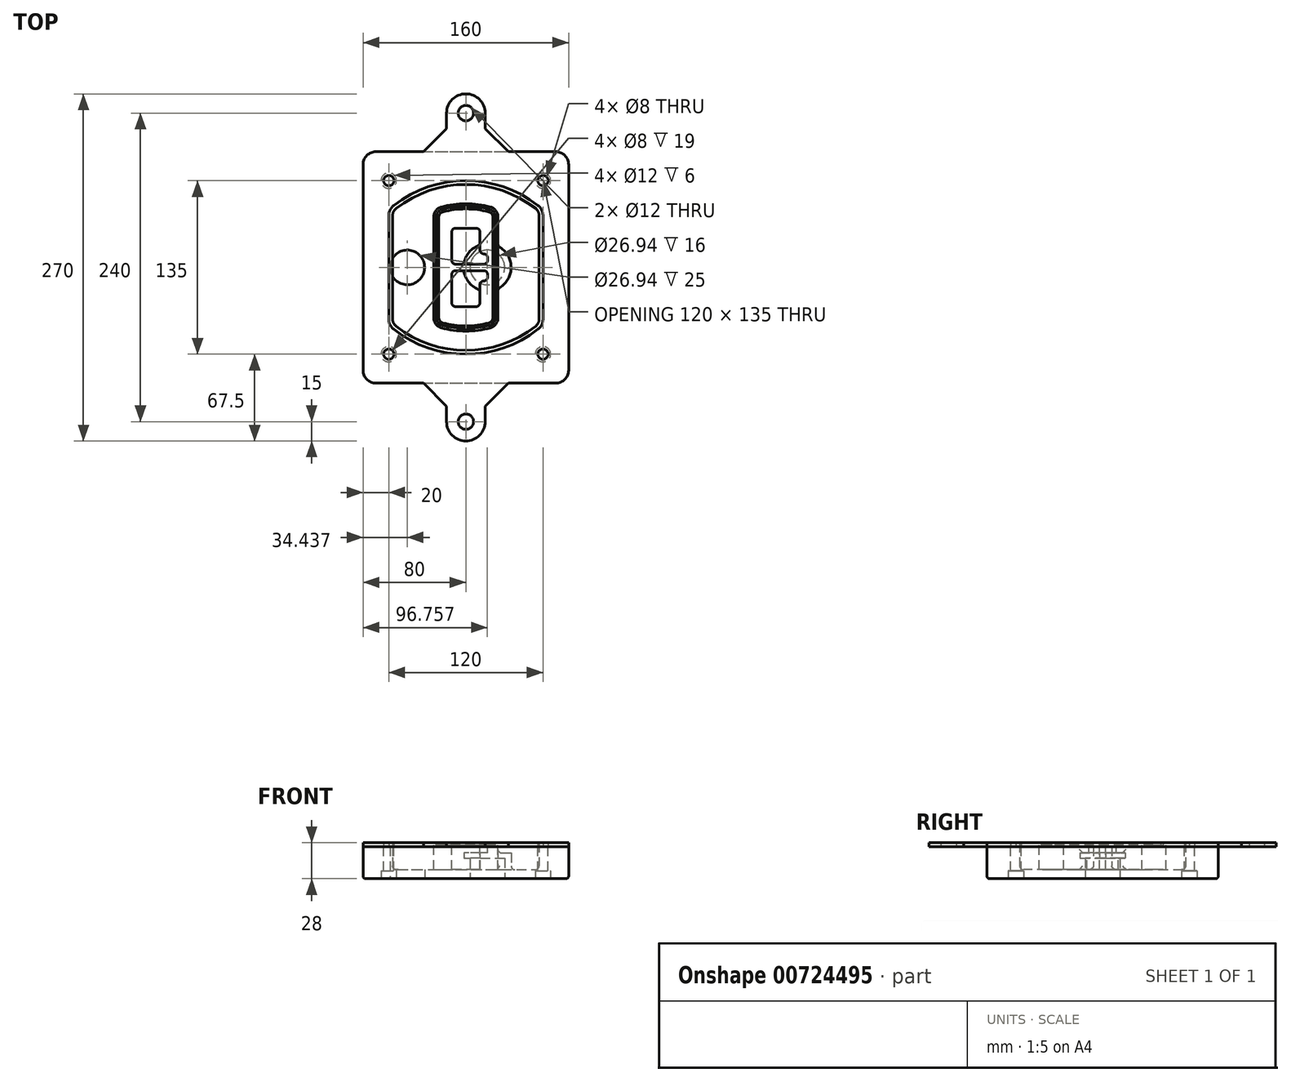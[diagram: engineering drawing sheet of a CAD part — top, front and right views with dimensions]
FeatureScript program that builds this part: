
annotation { "Feature Type Name" : "Feature", "Feature Type Description" : "" }
export const myFeature = defineFeature(function(context is Context, id is Id, definition is map)
    precondition{}
    {
        {
            var Q0;
            Q0=qCreatedBy(makeId("Top.planeOp"),FACE);
            var sketch = newSketch(context, id + "F0", { "sketchPlane" : qUnion([Q0])});
            skPoint(sketch, "E0.rect.middle", {"position": v(0, 0) * mm});
            skLineSegment(sketch, "E1.bottom", {"start": v(-70, -90) * mm, "end": v(70, -90) * mm});
            skLineSegment(sketch, "E1.top", {"start": v(-70, 90) * mm, "end": v(70, 90) * mm});
            skLineSegment(sketch, "E1.left", {"start": v(-80, -80) * mm, "end": v(-80, 80) * mm});
            skLineSegment(sketch, "E1.right", {"start": v(80, -80) * mm, "end": v(80, 80) * mm});
            skLineSegment(sketch, "E2", {"start": v(-80, 90) * mm, "end": v(80, -90) * mm, "construction": true});
            skLineSegment(sketch, "E3", {"start": v(80, 90) * mm, "end": v(-80, -90) * mm, "construction": true});
            skCircle(sketch, "E4", {"center": v(-60, 67.5) * mm, "radius": 4 * mm});
            skCircle(sketch, "E5", {"center": v(60, 67.5) * mm, "radius": 4 * mm});
            skCircle(sketch, "E6", {"center": v(60, -67.5) * mm, "radius": 4 * mm});
            skCircle(sketch, "E7", {"center": v(-60, -67.5) * mm, "radius": 4 * mm});
            skLineSegment(sketch, "E8", {"start": v(-60, 67.5) * mm, "end": v(60, 67.5) * mm, "construction": true});
            skLineSegment(sketch, "E9", {"start": v(60, 67.5) * mm, "end": v(60, -67.5) * mm, "construction": true});
            skLineSegment(sketch, "E10", {"start": v(60, -67.5) * mm, "end": v(-60, -67.5) * mm, "construction": true});
            skLineSegment(sketch, "E11", {"start": v(-60, -67.5) * mm, "end": v(-60, 67.5) * mm, "construction": true});
            skLineSegment(sketch, "E12", {"start": v(-60, 40.3) * mm, "end": v(-60, -40.3) * mm});
            skLineSegment(sketch, "E13", {"start": v(60, 40.3) * mm, "end": v(60, -40.3) * mm});
            skArc(sketch, "E14", {"start": v(56.15, 48.18) * mm, "mid": v(0, 67.5) * mm, "end": v(-56.15, 48.18) * mm});
            skArc(sketch, "E15", {"start": v(-56.15, -48.18) * mm, "mid": v(0, -67.5) * mm, "end": v(56.15, -48.18) * mm});
            skLineSegment(sketch, "E16", {"start": v(-60, 0) * mm, "end": v(60, 0) * mm, "construction": true});
            skPoint(sketch, "E17.visualSharp", {"position": v(-60, -45) * mm});
            skArc(sketch, "E17.filletArc", {"start": v(-60, -40.3) * mm, "mid": v(-58.99, -44.68) * mm, "end": v(-56.15, -48.18) * mm});
            skPoint(sketch, "E18.visualSharp", {"position": v(-60, 45) * mm});
            skArc(sketch, "E18.filletArc", {"start": v(-56.15, 48.18) * mm, "mid": v(-58.99, 44.68) * mm, "end": v(-60, 40.3) * mm});
            skPoint(sketch, "E19.visualSharp", {"position": v(60, 45) * mm});
            skArc(sketch, "E19.filletArc", {"start": v(60, 40.3) * mm, "mid": v(58.99, 44.68) * mm, "end": v(56.15, 48.18) * mm});
            skPoint(sketch, "E20.visualSharp", {"position": v(60, -45) * mm});
            skArc(sketch, "E20.filletArc", {"start": v(56.15, -48.18) * mm, "mid": v(58.99, -44.68) * mm, "end": v(60, -40.3) * mm});
            skPoint(sketch, "E21.visualSharp", {"position": v(-80, 90) * mm});
            skArc(sketch, "E21.filletArc", {"start": v(-70, 90) * mm, "mid": v(-77.07, 87.07) * mm, "end": v(-80, 80) * mm});
            skPoint(sketch, "E22.visualSharp", {"position": v(80, 90) * mm});
            skArc(sketch, "E22.filletArc", {"start": v(80, 80) * mm, "mid": v(77.07, 87.07) * mm, "end": v(70, 90) * mm});
            skPoint(sketch, "E23.visualSharp", {"position": v(80, -90) * mm});
            skArc(sketch, "E23.filletArc", {"start": v(70, -90) * mm, "mid": v(77.07, -87.07) * mm, "end": v(80, -80) * mm});
            skPoint(sketch, "E24.visualSharp", {"position": v(-80, -90) * mm});
            skArc(sketch, "E24.filletArc", {"start": v(-80, -80) * mm, "mid": v(-77.07, -87.07) * mm, "end": v(-70, -90) * mm});
            skArc(sketch, "E25.0", {"start": v(57, 40.3) * mm, "mid": v(56.3, 43.36) * mm, "end": v(54.3, 45.81) * mm});
            skLineSegment(sketch, "E25.1", {"start": v(57, 40.3) * mm, "end": v(57, -40.3) * mm});
            skArc(sketch, "E25.2", {"start": v(54.3, -45.81) * mm, "mid": v(56.3, -43.36) * mm, "end": v(57, -40.3) * mm});
            skArc(sketch, "E25.3", {"start": v(-54.3, -45.81) * mm, "mid": v(0, -64.5) * mm, "end": v(54.3, -45.81) * mm});
            skArc(sketch, "E25.4", {"start": v(-57, -40.3) * mm, "mid": v(-56.3, -43.36) * mm, "end": v(-54.3, -45.81) * mm});
            skArc(sketch, "E25.5", {"start": v(54.3, 45.81) * mm, "mid": v(0, 64.5) * mm, "end": v(-54.3, 45.81) * mm});
            skLineSegment(sketch, "E25.6", {"start": v(-57, 40.3) * mm, "end": v(-57, -40.3) * mm});
            skArc(sketch, "E25.7", {"start": v(-54.3, 45.81) * mm, "mid": v(-56.3, 43.36) * mm, "end": v(-57, 40.3) * mm});
            skArc(sketch, "E26.0", {"start": v(-58.62, 51.33) * mm, "mid": v(-62.58, 46.43) * mm, "end": v(-64, 40.3) * mm});
            skArc(sketch, "E26.1", {"start": v(58.62, 51.33) * mm, "mid": v(0, 71.5) * mm, "end": v(-58.62, 51.33) * mm});
            skArc(sketch, "E26.2", {"start": v(64, 40.3) * mm, "mid": v(62.58, 46.43) * mm, "end": v(58.62, 51.33) * mm});
            skLineSegment(sketch, "E26.3", {"start": v(64, 40.3) * mm, "end": v(64, -40.3) * mm});
            skArc(sketch, "E26.4", {"start": v(58.62, -51.33) * mm, "mid": v(62.58, -46.43) * mm, "end": v(64, -40.3) * mm});
            skLineSegment(sketch, "E26.5", {"start": v(-64, 40.3) * mm, "end": v(-64, -40.3) * mm});
            skArc(sketch, "E26.6", {"start": v(-58.62, -51.33) * mm, "mid": v(0, -71.5) * mm, "end": v(58.62, -51.33) * mm});
            skArc(sketch, "E26.7", {"start": v(-64, -40.3) * mm, "mid": v(-62.58, -46.43) * mm, "end": v(-58.62, -51.33) * mm});
            skSolve(sketch);
        }
        {
            var Q0;
            Q0=makeQuery(id+"F0.imprint","IMPRINT",FACE,{"disambiguationData":[TD([[makeQuery(id+"F0.imprint","IMPRINT",EDGE,{"derivedFrom":sQuery(id+"F0.wireOp",EDGE,"E1.bottom")}),1.0]])]});
            var Q1;
            Q1=makeQuery(id+"F0.imprint","IMPRINT",FACE,{"disambiguationData":[TD([[makeQuery(id+"F0.imprint","IMPRINT",EDGE,{"derivedFrom":sQuery(id+"F0.wireOp",EDGE,"E12")}),1.0]])]});
            var Q2;
            Q2=makeQuery(id+"F0.imprint","IMPRINT",FACE,{"disambiguationData":[TD([[makeQuery(id+"F0.imprint","IMPRINT",EDGE,{"derivedFrom":sQuery(id+"F0.wireOp",EDGE,"E25.0")}),1.0]])]});
            var Q3;
            Q3=makeQuery(id+"F0.imprint","IMPRINT",FACE,{"disambiguationData":[TD([[makeQuery(id+"F0.imprint","IMPRINT",EDGE,{"derivedFrom":sQuery(id+"F0.wireOp",EDGE,"E12")}),-1.0]])]});
            extrude(context, id + "F1", {"entities" : qUnion([Q0, Q1, Q2, Q3]), "oppositeDirection" : true, "depth" : 25 * mm});
        }
        {
            var Q0;
            Q0=makeQuery(id+"F0.imprint","IMPRINT",FACE,{"disambiguationData":[TD([[makeQuery(id+"F0.imprint","IMPRINT",EDGE,{"derivedFrom":sQuery(id+"F0.wireOp",EDGE,"E12")}),1.0]])]});
            extrude(context, id + "F2", {"entities" : qUnion([Q0]), "operationType" : NewBodyOperationType.ADD, "depth" : 3 * mm});
        }
        {
            var Q0;
            Q0=makeQuery(id+"F0.imprint","IMPRINT",FACE,{"disambiguationData":[TD([[makeQuery(id+"F0.imprint","IMPRINT",EDGE,{"derivedFrom":sQuery(id+"F0.wireOp",EDGE,"E25.0")}),1.0]])]});
            extrude(context, id + "F3", {"entities" : qUnion([Q0]), "operationType" : NewBodyOperationType.REMOVE, "oppositeDirection" : true, "depth" : 18 * mm});
        }
        {
            var Q0;
            Q0=makeQuery(id+"F2.opExtrude","CAP_FACE",FACE,{"disambiguationData":[OSD([sQuery(id+"F0.wireOp",EDGE,"E12"),sQuery(id+"F0.wireOp",EDGE,"E13"),sQuery(id+"F0.wireOp",EDGE,"E14"),sQuery(id+"F0.wireOp",EDGE,"E15"),sQuery(id+"F0.wireOp",EDGE,"E17.filletArc"),sQuery(id+"F0.wireOp",EDGE,"E18.filletArc"),sQuery(id+"F0.wireOp",EDGE,"E19.filletArc"),sQuery(id+"F0.wireOp",EDGE,"E20.filletArc"),sQuery(id+"F0.wireOp",EDGE,"E25.0"),sQuery(id+"F0.wireOp",EDGE,"E25.1"),sQuery(id+"F0.wireOp",EDGE,"E25.2"),sQuery(id+"F0.wireOp",EDGE,"E25.3"),sQuery(id+"F0.wireOp",EDGE,"E25.4"),sQuery(id+"F0.wireOp",EDGE,"E25.5"),sQuery(id+"F0.wireOp",EDGE,"E25.6"),sQuery(id+"F0.wireOp",EDGE,"E25.7")])],"isStart":false});
            var sketch = newSketch(context, id + "F4", { "sketchPlane" : qUnion([Q0])});
            skArc(sketch, "E27.0", {"start": v(-19.08, -46.97) * mm, "mid": v(0, -49.5) * mm, "end": v(19.08, -46.97) * mm});
            skArc(sketch, "E28.0", {"start": v(19.08, 46.97) * mm, "mid": v(0, 49.5) * mm, "end": v(-19.08, 46.97) * mm});
            skLineSegment(sketch, "E29", {"start": v(-25, 39.25) * mm, "end": v(-25, -39.25) * mm});
            skLineSegment(sketch, "E30", {"start": v(25, 39.25) * mm, "end": v(25, -39.25) * mm});
            skLineSegment(sketch, "E31", {"start": v(-25, 45.1) * mm, "end": v(25, 45.1) * mm, "construction": true});
            skLineSegment(sketch, "E32", {"start": v(-25, -45.1) * mm, "end": v(25, -45.1) * mm, "construction": true});
            skPoint(sketch, "E33.visualSharp", {"position": v(-25, 45.1) * mm});
            skArc(sketch, "E33.filletArc", {"start": v(-19.08, 46.97) * mm, "mid": v(-23.35, 44.11) * mm, "end": v(-25, 39.25) * mm});
            skPoint(sketch, "E34.visualSharp", {"position": v(25, 45.1) * mm});
            skArc(sketch, "E34.filletArc", {"start": v(25, 39.25) * mm, "mid": v(23.35, 44.11) * mm, "end": v(19.08, 46.97) * mm});
            skPoint(sketch, "E35.visualSharp", {"position": v(25, -45.1) * mm});
            skArc(sketch, "E35.filletArc", {"start": v(19.08, -46.97) * mm, "mid": v(23.35, -44.11) * mm, "end": v(25, -39.25) * mm});
            skPoint(sketch, "E36.visualSharp", {"position": v(-25, -45.1) * mm});
            skArc(sketch, "E36.filletArc", {"start": v(-25, -39.25) * mm, "mid": v(-23.35, -44.11) * mm, "end": v(-19.08, -46.97) * mm});
            skArc(sketch, "E37.0", {"start": v(54.3, 45.81) * mm, "mid": v(0, 64.5) * mm, "end": v(-54.3, 45.81) * mm});
            skArc(sketch, "E37.1", {"start": v(-54.3, 45.81) * mm, "mid": v(-56.3, 43.36) * mm, "end": v(-57, 40.3) * mm});
            skLineSegment(sketch, "E37.2", {"start": v(-57, 40.3) * mm, "end": v(-57, -40.3) * mm});
            skArc(sketch, "E37.3", {"start": v(-57, -40.3) * mm, "mid": v(-56.3, -43.36) * mm, "end": v(-54.3, -45.81) * mm});
            skArc(sketch, "E37.4", {"start": v(-54.3, -45.81) * mm, "mid": v(0, -64.5) * mm, "end": v(54.3, -45.81) * mm});
            skArc(sketch, "E37.5", {"start": v(54.3, -45.81) * mm, "mid": v(56.3, -43.36) * mm, "end": v(57, -40.3) * mm});
            skLineSegment(sketch, "E37.6", {"start": v(57, 40.3) * mm, "end": v(57, -40.3) * mm});
            skArc(sketch, "E37.7", {"start": v(57, 40.3) * mm, "mid": v(56.3, 43.36) * mm, "end": v(54.3, 45.81) * mm});
            skLineSegment(sketch, "E38.0", {"start": v(23, 39.25) * mm, "end": v(23, -39.25) * mm});
            skArc(sketch, "E38.1", {"start": v(18.56, -45.04) * mm, "mid": v(21.76, -42.9) * mm, "end": v(23, -39.25) * mm});
            skArc(sketch, "E38.2", {"start": v(-18.56, -45.04) * mm, "mid": v(0, -47.5) * mm, "end": v(18.56, -45.04) * mm});
            skArc(sketch, "E38.3", {"start": v(-23, -39.25) * mm, "mid": v(-21.76, -42.9) * mm, "end": v(-18.56, -45.04) * mm});
            skLineSegment(sketch, "E38.4", {"start": v(-23, 39.25) * mm, "end": v(-23, -39.25) * mm});
            skArc(sketch, "E38.5", {"start": v(23, 39.25) * mm, "mid": v(21.76, 42.9) * mm, "end": v(18.56, 45.04) * mm});
            skArc(sketch, "E38.6", {"start": v(-18.56, 45.04) * mm, "mid": v(-21.76, 42.9) * mm, "end": v(-23, 39.25) * mm});
            skArc(sketch, "E38.7", {"start": v(18.56, 45.04) * mm, "mid": v(0, 47.5) * mm, "end": v(-18.56, 45.04) * mm});
            skArc(sketch, "E39.0", {"start": v(21, 39.25) * mm, "mid": v(20.18, 41.68) * mm, "end": v(18.04, 43.1) * mm});
            skLineSegment(sketch, "E39.1", {"start": v(21, 39.25) * mm, "end": v(21, -39.25) * mm});
            skArc(sketch, "E39.2", {"start": v(18.04, -43.1) * mm, "mid": v(20.18, -41.68) * mm, "end": v(21, -39.25) * mm});
            skArc(sketch, "E39.3", {"start": v(-18.04, -43.1) * mm, "mid": v(0, -45.5) * mm, "end": v(18.04, -43.1) * mm});
            skArc(sketch, "E39.4", {"start": v(-21, -39.25) * mm, "mid": v(-20.18, -41.68) * mm, "end": v(-18.04, -43.1) * mm});
            skArc(sketch, "E39.5", {"start": v(18.04, 43.1) * mm, "mid": v(0, 45.5) * mm, "end": v(-18.04, 43.1) * mm});
            skLineSegment(sketch, "E39.6", {"start": v(-21, 39.25) * mm, "end": v(-21, -39.25) * mm});
            skArc(sketch, "E39.7", {"start": v(-18.04, 43.1) * mm, "mid": v(-20.18, 41.68) * mm, "end": v(-21, 39.25) * mm});
            skLineSegment(sketch, "E40", {"start": v(-25, 0) * mm, "end": v(25, 0) * mm, "construction": true});
            skLineSegment(sketch, "E41", {"start": v(-11, 5.5) * mm, "end": v(-11, 27.5) * mm});
            skLineSegment(sketch, "E42", {"start": v(-8, 30.5) * mm, "end": v(8, 30.5) * mm});
            skLineSegment(sketch, "E43", {"start": v(11, 27.5) * mm, "end": v(11, 13.5) * mm});
            skLineSegment(sketch, "E44", {"start": v(14, 10.5) * mm, "end": v(14, 10.5) * mm});
            skLineSegment(sketch, "E45", {"start": v(17, 7.5) * mm, "end": v(17, 5.5) * mm});
            skLineSegment(sketch, "E46", {"start": v(14, 2.5) * mm, "end": v(-8, 2.5) * mm});
            skPoint(sketch, "E47.visualSharp", {"position": v(-11, 30.5) * mm});
            skArc(sketch, "E47.filletArc", {"start": v(-8, 30.5) * mm, "mid": v(-10.12, 29.62) * mm, "end": v(-11, 27.5) * mm});
            skPoint(sketch, "E48.visualSharp", {"position": v(11, 30.5) * mm});
            skArc(sketch, "E48.filletArc", {"start": v(11, 27.5) * mm, "mid": v(10.12, 29.62) * mm, "end": v(8, 30.5) * mm});
            skPoint(sketch, "E49.visualSharp", {"position": v(11, 10.5) * mm});
            skArc(sketch, "E49.filletArc", {"start": v(11, 13.5) * mm, "mid": v(11.88, 11.38) * mm, "end": v(14, 10.5) * mm});
            skPoint(sketch, "E50.visualSharp", {"position": v(17, 10.5) * mm});
            skArc(sketch, "E50.filletArc", {"start": v(17, 7.5) * mm, "mid": v(16.12, 9.62) * mm, "end": v(14, 10.5) * mm});
            skPoint(sketch, "E51.visualSharp", {"position": v(17, 2.5) * mm});
            skArc(sketch, "E51.filletArc", {"start": v(14, 2.5) * mm, "mid": v(16.12, 3.38) * mm, "end": v(17, 5.5) * mm});
            skPoint(sketch, "E52.visualSharp", {"position": v(-11, 2.5) * mm});
            skArc(sketch, "E52.filletArc", {"start": v(-11, 5.5) * mm, "mid": v(-10.12, 3.38) * mm, "end": v(-8, 2.5) * mm});
            skLineSegment(sketch, "E53.0.MirrorCS", {"start": v(14, -2.5) * mm, "end": v(-8, -2.5) * mm});
            skArc(sketch, "E54.0.MirrorCS", {"start": v(-11, -5.5) * mm, "mid": v(-10.12, -3.38) * mm, "end": v(-8, -2.5) * mm});
            skLineSegment(sketch, "E55.0.MirrorCS", {"start": v(-11, -5.5) * mm, "end": v(-11, -27.5) * mm});
            skArc(sketch, "E56.0.MirrorCS", {"start": v(-8, -30.5) * mm, "mid": v(-10.12, -29.62) * mm, "end": v(-11, -27.5) * mm});
            skLineSegment(sketch, "E57.0.MirrorCS", {"start": v(-8, -30.5) * mm, "end": v(8, -30.5) * mm});
            skArc(sketch, "E58.0.MirrorCS", {"start": v(11, -27.5) * mm, "mid": v(10.12, -29.62) * mm, "end": v(8, -30.5) * mm});
            skLineSegment(sketch, "E59.0.MirrorCS", {"start": v(11, -27.5) * mm, "end": v(11, -13.5) * mm});
            skArc(sketch, "E60.0.MirrorCS", {"start": v(11, -13.5) * mm, "mid": v(11.88, -11.38) * mm, "end": v(14, -10.5) * mm});
            skArc(sketch, "E61.0.MirrorCS", {"start": v(17, -7.5) * mm, "mid": v(16.12, -9.62) * mm, "end": v(14, -10.5) * mm});
            skLineSegment(sketch, "E62.0.MirrorCS", {"start": v(17, -7.5) * mm, "end": v(17, -5.5) * mm});
            skArc(sketch, "E63.0.MirrorCS", {"start": v(14, -2.5) * mm, "mid": v(16.12, -3.38) * mm, "end": v(17, -5.5) * mm});
            skSolve(sketch);
        }
        {
            var Q0;
            Q0=makeQuery(id+"F4.imprint","IMPRINT",FACE,{"disambiguationData":[TD([[makeQuery(id+"F4.imprint","IMPRINT",EDGE,{"derivedFrom":sQuery(id+"F4.wireOp",EDGE,"E27.0")}),1.0]])]});
            var Q1;
            Q1=makeQuery(id+"F4.imprint","IMPRINT",FACE,{"disambiguationData":[TD([[makeQuery(id+"F4.imprint","IMPRINT",EDGE,{"derivedFrom":sQuery(id+"F4.wireOp",EDGE,"E38.0")}),-1.0]])]});
            var Q2;
            Q2=makeQuery(id+"F4.imprint","IMPRINT",FACE,{"disambiguationData":[TD([[makeQuery(id+"F4.imprint","IMPRINT",EDGE,{"derivedFrom":sQuery(id+"F4.wireOp",EDGE,"E39.0")}),1.0]])]});
            extrude(context, id + "F5", {"entities" : qUnion([Q0, Q1, Q2]), "operationType" : NewBodyOperationType.ADD, "endBound" : BoundingType.UP_TO_NEXT, "oppositeDirection" : true, "depth" : 25 * mm});
        }
        {
            var Q0;
            Q0=makeQuery(id+"F4.imprint","IMPRINT",FACE,{"disambiguationData":[TD([[makeQuery(id+"F4.imprint","IMPRINT",EDGE,{"derivedFrom":sQuery(id+"F4.wireOp",EDGE,"E38.0")}),-1.0]])]});
            extrude(context, id + "F6", {"entities" : qUnion([Q0]), "operationType" : NewBodyOperationType.REMOVE, "oppositeDirection" : true, "depth" : 2 * mm});
        }
        {
            var Q0;
            Q0=makeQuery(id+"F1.opExtrude","CAP_FACE",FACE,{"disambiguationData":[OSD([sQuery(id+"F0.wireOp",EDGE,"E1.bottom"),sQuery(id+"F0.wireOp",EDGE,"E1.top"),sQuery(id+"F0.wireOp",EDGE,"E1.left"),sQuery(id+"F0.wireOp",EDGE,"E1.right"),sQuery(id+"F0.wireOp",EDGE,"E4"),sQuery(id+"F0.wireOp",EDGE,"E5"),sQuery(id+"F0.wireOp",EDGE,"E6"),sQuery(id+"F0.wireOp",EDGE,"E7"),sQuery(id+"F0.wireOp",EDGE,"E21.filletArc"),sQuery(id+"F0.wireOp",EDGE,"E22.filletArc"),sQuery(id+"F0.wireOp",EDGE,"E23.filletArc"),sQuery(id+"F0.wireOp",EDGE,"E24.filletArc")])],"isStart":false});
            var sketch = newSketch(context, id + "F7", { "sketchPlane" : qUnion([Q0])});
            skCircle(sketch, "E64", {"center": v(16.76, 0) * mm, "radius": 13.47 * mm});
            skCircle(sketch, "E65", {"center": v(-45.56, 0) * mm, "radius": 13.47 * mm});
            skLineSegment(sketch, "E66", {"start": v(80, 0) * mm, "end": v(-80, 0) * mm});
            skCircle(sketch, "E67", {"center": v(16.76, 0) * mm, "radius": 18.47 * mm});
            skCircle(sketch, "E68", {"center": v(60, -67.5) * mm, "radius": 6 * mm});
            skCircle(sketch, "E69", {"center": v(-60, -67.5) * mm, "radius": 6 * mm});
            skCircle(sketch, "E70", {"center": v(-60, 67.5) * mm, "radius": 6 * mm});
            skCircle(sketch, "E71", {"center": v(60, 67.5) * mm, "radius": 6 * mm});
            skSolve(sketch);
        }
        {
            var Q0;
            {var subQ1=sQuery(id+"F7.wireOp",EDGE,"E66");var subQ4=sQuery(id+"F7.wireOp",EDGE,"E64");var subQ6=makeQuery(id+"F7.imprint","INTERSECT",VERTEX,{"disambiguationData":[OD(0.0)],"derivedFrom":[subQ4,subQ1]});Q0=makeQuery(id+"F7.imprint","IMPRINT",FACE,{"disambiguationData":[TD([[makeQuery(id+"F7.imprint","IMPRINT",EDGE,{"disambiguationData":[TD([[subQ6,-1.0]])],"derivedFrom":subQ4}),-1.0]])]});}
            var Q1;
            {var subQ0=sQuery(id+"F7.wireOp",EDGE,"E66");var subQ1=sQuery(id+"F7.wireOp",EDGE,"E64");var subQ3=makeQuery(id+"F7.imprint","INTERSECT",VERTEX,{"disambiguationData":[OD(0.0)],"derivedFrom":[subQ1,subQ0]});Q1=makeQuery(id+"F7.imprint","IMPRINT",FACE,{"disambiguationData":[TD([[makeQuery(id+"F7.imprint","IMPRINT",EDGE,{"disambiguationData":[TD([[subQ3,-1.0]])],"derivedFrom":subQ1}),1.0]])]});}
            var Q2;
            {var subQ0=sQuery(id+"F7.wireOp",EDGE,"E66");var subQ1=sQuery(id+"F7.wireOp",EDGE,"E64");var subQ3=makeQuery(id+"F7.imprint","INTERSECT",VERTEX,{"disambiguationData":[OD(0.0)],"derivedFrom":[subQ1,subQ0]});Q2=makeQuery(id+"F7.imprint","IMPRINT",FACE,{"disambiguationData":[TD([[makeQuery(id+"F7.imprint","IMPRINT",EDGE,{"disambiguationData":[TD([[subQ3,1.0]])],"derivedFrom":subQ1}),1.0]])]});}
            var Q3;
            {var subQ1=sQuery(id+"F7.wireOp",EDGE,"E66");var subQ4=sQuery(id+"F7.wireOp",EDGE,"E64");var subQ6=makeQuery(id+"F7.imprint","INTERSECT",VERTEX,{"disambiguationData":[OD(0.0)],"derivedFrom":[subQ4,subQ1]});Q3=makeQuery(id+"F7.imprint","IMPRINT",FACE,{"disambiguationData":[TD([[makeQuery(id+"F7.imprint","IMPRINT",EDGE,{"disambiguationData":[TD([[subQ6,1.0]])],"derivedFrom":subQ4}),-1.0]])]});}
            extrude(context, id + "F8", {"entities" : qUnion([Q0, Q1, Q2, Q3]), "operationType" : NewBodyOperationType.ADD, "oppositeDirection" : true, "depth" : 20 * mm});
        }
        {
            var Q0;
            {var subQ0=sQuery(id+"F7.wireOp",EDGE,"E66");var subQ1=sQuery(id+"F7.wireOp",EDGE,"E64");var subQ3=makeQuery(id+"F7.imprint","INTERSECT",VERTEX,{"disambiguationData":[OD(0.0)],"derivedFrom":[subQ1,subQ0]});Q0=makeQuery(id+"F7.imprint","IMPRINT",FACE,{"disambiguationData":[TD([[makeQuery(id+"F7.imprint","IMPRINT",EDGE,{"disambiguationData":[TD([[subQ3,-1.0]])],"derivedFrom":subQ1}),1.0]])]});}
            var Q1;
            {var subQ0=sQuery(id+"F7.wireOp",EDGE,"E66");var subQ1=sQuery(id+"F7.wireOp",EDGE,"E64");var subQ3=makeQuery(id+"F7.imprint","INTERSECT",VERTEX,{"disambiguationData":[OD(0.0)],"derivedFrom":[subQ1,subQ0]});Q1=makeQuery(id+"F7.imprint","IMPRINT",FACE,{"disambiguationData":[TD([[makeQuery(id+"F7.imprint","IMPRINT",EDGE,{"disambiguationData":[TD([[subQ3,1.0]])],"derivedFrom":subQ1}),1.0]])]});}
            extrude(context, id + "F9", {"entities" : qUnion([Q0, Q1]), "operationType" : NewBodyOperationType.REMOVE, "oppositeDirection" : true, "depth" : 16 * mm});
        }
        {
            var Q0;
            {var subQ0=sQuery(id+"F7.wireOp",EDGE,"E66");var subQ1=sQuery(id+"F7.wireOp",EDGE,"E65");var subQ3=makeQuery(id+"F7.imprint","INTERSECT",VERTEX,{"disambiguationData":[OD(0.0)],"derivedFrom":[subQ1,subQ0]});Q0=makeQuery(id+"F7.imprint","IMPRINT",FACE,{"disambiguationData":[TD([[makeQuery(id+"F7.imprint","IMPRINT",EDGE,{"disambiguationData":[TD([[subQ3,-1.0]])],"derivedFrom":subQ1}),1.0]])]});}
            var Q1;
            {var subQ0=sQuery(id+"F7.wireOp",EDGE,"E66");var subQ1=sQuery(id+"F7.wireOp",EDGE,"E65");var subQ3=makeQuery(id+"F7.imprint","INTERSECT",VERTEX,{"disambiguationData":[OD(0.0)],"derivedFrom":[subQ1,subQ0]});Q1=makeQuery(id+"F7.imprint","IMPRINT",FACE,{"disambiguationData":[TD([[makeQuery(id+"F7.imprint","IMPRINT",EDGE,{"disambiguationData":[TD([[subQ3,1.0]])],"derivedFrom":subQ1}),1.0]])]});}
            extrude(context, id + "F10", {"entities" : qUnion([Q0, Q1]), "operationType" : NewBodyOperationType.REMOVE, "oppositeDirection" : true, "depth" : 25 * mm});
        }
        {
            var Q0;
            Q0=makeQuery(id+"F7.imprint","IMPRINT",FACE,{"disambiguationData":[TD([[makeQuery(id+"F7.imprint","IMPRINT",EDGE,{"derivedFrom":sQuery(id+"F7.wireOp",EDGE,"E68")}),1.0]])]});
            var Q1;
            Q1=makeQuery(id+"F7.imprint","IMPRINT",FACE,{"disambiguationData":[TD([[makeQuery(id+"F7.imprint","IMPRINT",EDGE,{"derivedFrom":makeQuery(id+"F1.opExtrude","CAP_EDGE",EDGE,{"disambiguationData":[OSD([sQuery(id+"F0.wireOp",EDGE,"E5")])],"isStart":false})}),-1.0]])]});
            var Q2;
            Q2=makeQuery(id+"F7.imprint","IMPRINT",FACE,{"disambiguationData":[TD([[makeQuery(id+"F7.imprint","IMPRINT",EDGE,{"derivedFrom":sQuery(id+"F7.wireOp",EDGE,"E69")}),1.0]])]});
            var Q3;
            Q3=makeQuery(id+"F7.imprint","IMPRINT",FACE,{"disambiguationData":[TD([[makeQuery(id+"F7.imprint","IMPRINT",EDGE,{"derivedFrom":makeQuery(id+"F1.opExtrude","CAP_EDGE",EDGE,{"disambiguationData":[OSD([sQuery(id+"F0.wireOp",EDGE,"E4")])],"isStart":false})}),-1.0]])]});
            var Q4;
            Q4=makeQuery(id+"F7.imprint","IMPRINT",FACE,{"disambiguationData":[TD([[makeQuery(id+"F7.imprint","IMPRINT",EDGE,{"derivedFrom":sQuery(id+"F7.wireOp",EDGE,"E70")}),1.0]])]});
            var Q5;
            Q5=makeQuery(id+"F7.imprint","IMPRINT",FACE,{"disambiguationData":[TD([[makeQuery(id+"F7.imprint","IMPRINT",EDGE,{"derivedFrom":makeQuery(id+"F1.opExtrude","CAP_EDGE",EDGE,{"disambiguationData":[OSD([sQuery(id+"F0.wireOp",EDGE,"E7")])],"isStart":false})}),-1.0]])]});
            var Q6;
            Q6=makeQuery(id+"F7.imprint","IMPRINT",FACE,{"disambiguationData":[TD([[makeQuery(id+"F7.imprint","IMPRINT",EDGE,{"derivedFrom":sQuery(id+"F7.wireOp",EDGE,"E71")}),1.0]])]});
            var Q7;
            Q7=makeQuery(id+"F7.imprint","IMPRINT",FACE,{"disambiguationData":[TD([[makeQuery(id+"F7.imprint","IMPRINT",EDGE,{"derivedFrom":makeQuery(id+"F1.opExtrude","CAP_EDGE",EDGE,{"disambiguationData":[OSD([sQuery(id+"F0.wireOp",EDGE,"E6")])],"isStart":false})}),-1.0]])]});
            extrude(context, id + "F11", {"entities" : qUnion([Q0, Q1, Q2, Q3, Q4, Q5, Q6, Q7]), "operationType" : NewBodyOperationType.REMOVE, "oppositeDirection" : true, "depth" : 6 * mm});
        }
        {
            var Q0;
            Q0=makeQuery(id+"F9.boolean.opBoolean","COPY",FACE,{"derivedFrom":makeQuery(id+"F9.opExtrude","CAP_FACE",FACE,{"disambiguationData":[OSD([sQuery(id+"F7.wireOp",EDGE,"E64")])],"isStart":false})});
            var sketch = newSketch(context, id + "F12", { "sketchPlane" : qUnion([Q0])});
            skArc(sketch, "E72.0", {"start": v(11, 17.55) * mm, "mid": v(2.57, 11.82) * mm, "end": v(-1.54, 2.5) * mm});
            skArc(sketch, "E72.1", {"start": v(-1.54, -2.5) * mm, "mid": v(2.57, -11.82) * mm, "end": v(11, -17.55) * mm});
            skLineSegment(sketch, "E73", {"start": v(-1.54, -2.5) * mm, "end": v(14, -2.5) * mm});
            skLineSegment(sketch, "E74.0", {"start": v(14, 2.5) * mm, "end": v(-1.54, 2.5) * mm});
            skArc(sketch, "E74.1", {"start": v(14, 2.5) * mm, "mid": v(16.12, 3.38) * mm, "end": v(17, 5.5) * mm});
            skLineSegment(sketch, "E74.2", {"start": v(17, 7.5) * mm, "end": v(17, 5.5) * mm});
            skArc(sketch, "E74.3", {"start": v(17, 7.5) * mm, "mid": v(16.12, 9.62) * mm, "end": v(14, 10.5) * mm});
            skArc(sketch, "E74.4", {"start": v(11, 13.5) * mm, "mid": v(11.88, 11.38) * mm, "end": v(14, 10.5) * mm});
            skLineSegment(sketch, "E74.5", {"start": v(11, 17.55) * mm, "end": v(11, 13.5) * mm});
            skLineSegment(sketch, "E74.7", {"start": v(14, -2.5) * mm, "end": v(-1.54, -2.5) * mm});
            skArc(sketch, "E74.8", {"start": v(14, -2.5) * mm, "mid": v(16.12, -3.38) * mm, "end": v(17, -5.5) * mm});
            skLineSegment(sketch, "E74.9", {"start": v(17, -7.5) * mm, "end": v(17, -5.5) * mm});
            skArc(sketch, "E74.10", {"start": v(17, -7.5) * mm, "mid": v(16.12, -9.62) * mm, "end": v(14, -10.5) * mm});
            skArc(sketch, "E74.11", {"start": v(11, -13.5) * mm, "mid": v(11.88, -11.38) * mm, "end": v(14, -10.5) * mm});
            skLineSegment(sketch, "E74.12", {"start": v(11, -17.55) * mm, "end": v(11, -13.5) * mm});
            skPoint(sketch, "E75.orphan", {"position": v(11, -27.5) * mm});
            skPoint(sketch, "E76.orphan", {"position": v(-8, -2.5) * mm});
            skPoint(sketch, "E77.orphan", {"position": v(-8, 2.5) * mm});
            skPoint(sketch, "E78.orphan", {"position": v(11, 27.5) * mm});
            skSolve(sketch);
        }
        {
            var Q0;
            {var subQ7=sQuery(id+"F12.wireOp",EDGE,"E72.0");var subQ14=sQuery(id+"F12.wireOp",EDGE,"E72.1");var subQ16=sQuery(id+"F12.wireOp",EDGE,"E74.1");var subQ18=sQuery(id+"F12.wireOp",EDGE,"E74.8");Q0=qUnion([makeQuery(id+"F12.imprint","IMPRINT",FACE,{"disambiguationData":[TD([[makeQuery(id+"F12.imprint","IMPRINT",EDGE,{"derivedFrom":subQ7}),1.0]])]}),makeQuery(id+"F12.imprint","IMPRINT",FACE,{"disambiguationData":[TD([[makeQuery(id+"F12.imprint","IMPRINT",EDGE,{"derivedFrom":subQ14}),1.0]])]}),makeQuery(id+"F12.imprint","IMPRINT",FACE,{"disambiguationData":[TD([[makeQuery(id+"F12.imprint","IMPRINT",EDGE,{"derivedFrom":subQ16}),1.0]])]}),makeQuery(id+"F12.imprint","IMPRINT",FACE,{"disambiguationData":[TD([[makeQuery(id+"F12.imprint","IMPRINT",EDGE,{"derivedFrom":subQ18}),-1.0]])]})]);}
            var Q1;
            Q1=makeQuery(id+"F5.boolean.opBoolean","SPLIT",FACE,{"disambiguationData":[TD([makeQuery(id+"F5.opExtrude","SWEPT_FACE",FACE,{"disambiguationData":[OSD([sQuery(id+"F4.wireOp",EDGE,"E41")])]})])],"derivedFrom":makeQuery(id+"F3.boolean.opBoolean","COPY",FACE,{"derivedFrom":makeQuery(id+"F3.opExtrude","CAP_FACE",FACE,{"disambiguationData":[OSD([sQuery(id+"F0.wireOp",EDGE,"E25.0"),sQuery(id+"F0.wireOp",EDGE,"E25.1"),sQuery(id+"F0.wireOp",EDGE,"E25.2"),sQuery(id+"F0.wireOp",EDGE,"E25.3"),sQuery(id+"F0.wireOp",EDGE,"E25.4"),sQuery(id+"F0.wireOp",EDGE,"E25.5"),sQuery(id+"F0.wireOp",EDGE,"E25.6"),sQuery(id+"F0.wireOp",EDGE,"E25.7")])],"isStart":false})})});
            extrude(context, id + "F13", {"entities" : qUnion([Q0]), "operationType" : NewBodyOperationType.REMOVE, "endBound" : BoundingType.UP_TO_SURFACE, "endBoundEntityFace" : qUnion([Q1]), "depth" : 25 * mm});
        }
        {
            var Q0;
            Q0=makeQuery(id+"F3.boolean.opBoolean","COPY",EDGE,{"derivedFrom":makeQuery(id+"F3.opExtrude","CAP_EDGE",EDGE,{"disambiguationData":[OSD([sQuery(id+"F0.wireOp",EDGE,"E25.6")])],"isStart":false})});
            var Q1;
            Q1=makeQuery(id+"F8.boolean.opBoolean","INTERSECT",EDGE,{"derivedFrom":[makeQuery(id+"F5.opExtrude","SWEPT_FACE",FACE,{"disambiguationData":[OSD([sQuery(id+"F4.wireOp",EDGE,"E30")])]}),makeQuery(id+"F8.opExtrude","CAP_FACE",FACE,{"disambiguationData":[OSD([sQuery(id+"F7.wireOp",EDGE,"E67")])],"isStart":false})]});
            var Q2;
            Q2=makeQuery(id+"F8.boolean.opBoolean","INTERSECT",EDGE,{"disambiguationData":[OD(1.0)],"derivedFrom":[makeQuery(id+"F5.opExtrude","SWEPT_FACE",FACE,{"disambiguationData":[OSD([sQuery(id+"F4.wireOp",EDGE,"E30")])]}),makeQuery(id+"F8.opExtrude","SWEPT_FACE",FACE,{"disambiguationData":[OSD([sQuery(id+"F7.wireOp",EDGE,"E67")])]})]});
            var Q3;
            {var subQ0=makeQuery(id+"F3.boolean.opBoolean","COPY",FACE,{"derivedFrom":makeQuery(id+"F3.opExtrude","CAP_FACE",FACE,{"disambiguationData":[OSD([sQuery(id+"F0.wireOp",EDGE,"E25.0"),sQuery(id+"F0.wireOp",EDGE,"E25.1"),sQuery(id+"F0.wireOp",EDGE,"E25.2"),sQuery(id+"F0.wireOp",EDGE,"E25.3"),sQuery(id+"F0.wireOp",EDGE,"E25.4"),sQuery(id+"F0.wireOp",EDGE,"E25.5"),sQuery(id+"F0.wireOp",EDGE,"E25.6"),sQuery(id+"F0.wireOp",EDGE,"E25.7")])],"isStart":false})});var subQ1=sQuery(id+"F4.wireOp",EDGE,"E30");Q3=makeQuery(id+"F8.boolean.opBoolean","SPLIT",EDGE,{"disambiguationData":[TD([makeQuery(id+"F5.opExtrude","SWEPT_FACE",FACE,{"disambiguationData":[OSD([sQuery(id+"F4.wireOp",EDGE,"E35.filletArc")])]})])],"derivedFrom":makeQuery(id+"F5.opExtrude","TWEAK_EDGE",EDGE,{"derivedFrom":[subQ0,makeQuery(id+"F4.imprint","IMPRINT",EDGE,{"derivedFrom":subQ1})]})});}
            var Q4;
            {var subQ0=sQuery(id+"F0.wireOp",EDGE,"E25.0");var subQ1=sQuery(id+"F0.wireOp",EDGE,"E25.1");var subQ2=sQuery(id+"F0.wireOp",EDGE,"E25.2");var subQ3=sQuery(id+"F0.wireOp",EDGE,"E25.3");var subQ4=sQuery(id+"F0.wireOp",EDGE,"E25.4");var subQ5=sQuery(id+"F0.wireOp",EDGE,"E25.5");var subQ6=sQuery(id+"F0.wireOp",EDGE,"E25.6");var subQ7=sQuery(id+"F0.wireOp",EDGE,"E25.7");Q4=makeQuery(id+"F8.boolean.opBoolean","INTERSECT",EDGE,{"derivedFrom":[makeQuery(id+"F5.boolean.opBoolean","SPLIT",FACE,{"disambiguationData":[TD([makeQuery(id+"F2.opExtrude","SWEPT_FACE",FACE,{"disambiguationData":[OSD([subQ0])]})])],"derivedFrom":makeQuery(id+"F3.boolean.opBoolean","COPY",FACE,{"derivedFrom":makeQuery(id+"F3.opExtrude","CAP_FACE",FACE,{"disambiguationData":[OSD([subQ0,subQ1,subQ2,subQ3,subQ4,subQ5,subQ6,subQ7])],"isStart":false})})}),makeQuery(id+"F8.opExtrude","SWEPT_FACE",FACE,{"disambiguationData":[OSD([sQuery(id+"F7.wireOp",EDGE,"E67")])]})]});}
            var Q5;
            Q5=makeQuery(id+"F8.boolean.opBoolean","INTERSECT",EDGE,{"disambiguationData":[OD(0.0)],"derivedFrom":[makeQuery(id+"F5.opExtrude","SWEPT_FACE",FACE,{"disambiguationData":[OSD([sQuery(id+"F4.wireOp",EDGE,"E30")])]}),makeQuery(id+"F8.opExtrude","SWEPT_FACE",FACE,{"disambiguationData":[OSD([sQuery(id+"F7.wireOp",EDGE,"E67")])]})]});
            fillet(context, id + "F14", {"entities" : qUnion([Q0, Q1, Q2, Q3, Q4, Q5]), "radius" : 3 * mm, "tangentPropagation" : true, "allowEdgeOverflow" : false});
        }
        {
            var Q0;
            Q0=makeQuery(id+"F1.opExtrude","CAP_EDGE",EDGE,{"disambiguationData":[OSD([sQuery(id+"F0.wireOp",EDGE,"E1.bottom")])],"isStart":false});
            fillet(context, id + "F15", {"entities" : qUnion([Q0]), "radius" : 2 * mm, "tangentPropagation" : true, "allowEdgeOverflow" : false});
        }
        {
            var Q0;
            Q0=qCreatedBy(makeId("Top.planeOp"),FACE);
            var sketch = newSketch(context, id + "F16", { "sketchPlane" : qUnion([Q0])});
            skArc(sketch, "E79.0", {"start": v(-70, 90) * mm, "mid": v(-77.07, 87.07) * mm, "end": v(-80, 80) * mm});
            skLineSegment(sketch, "E79.1", {"start": v(-70, 90) * mm, "end": v(70, 90) * mm});
            skLineSegment(sketch, "E79.2", {"start": v(-80, -80) * mm, "end": v(-80, 80) * mm});
            skCircle(sketch, "E79.3", {"center": v(-60, 67.5) * mm, "radius": 4 * mm});
            skArc(sketch, "E79.4", {"start": v(56.15, 48.18) * mm, "mid": v(0, 67.5) * mm, "end": v(-56.15, 48.18) * mm});
            skArc(sketch, "E79.5", {"start": v(-56.15, 48.18) * mm, "mid": v(-58.99, 44.68) * mm, "end": v(-60, 40.3) * mm});
            skLineSegment(sketch, "E79.6", {"start": v(-60, 40.3) * mm, "end": v(-60, -40.3) * mm});
            skArc(sketch, "E79.7", {"start": v(60, 40.3) * mm, "mid": v(58.99, 44.68) * mm, "end": v(56.15, 48.18) * mm});
            skLineSegment(sketch, "E79.8", {"start": v(60, 40.3) * mm, "end": v(60, -40.3) * mm});
            skArc(sketch, "E79.9", {"start": v(56.15, -48.18) * mm, "mid": v(58.99, -44.68) * mm, "end": v(60, -40.3) * mm});
            skArc(sketch, "E79.10", {"start": v(-56.15, -48.18) * mm, "mid": v(0, -67.5) * mm, "end": v(56.15, -48.18) * mm});
            skArc(sketch, "E79.11", {"start": v(-60, -40.3) * mm, "mid": v(-58.99, -44.68) * mm, "end": v(-56.15, -48.18) * mm});
            skArc(sketch, "E79.12", {"start": v(-80, -80) * mm, "mid": v(-77.07, -87.07) * mm, "end": v(-70, -90) * mm});
            skLineSegment(sketch, "E79.13", {"start": v(-70, -90) * mm, "end": v(70, -90) * mm});
            skCircle(sketch, "E79.14", {"center": v(-60, -67.5) * mm, "radius": 4 * mm});
            skCircle(sketch, "E79.15", {"center": v(60, -67.5) * mm, "radius": 4 * mm});
            skArc(sketch, "E79.16", {"start": v(70, -90) * mm, "mid": v(77.07, -87.07) * mm, "end": v(80, -80) * mm});
            skLineSegment(sketch, "E79.17", {"start": v(80, -80) * mm, "end": v(80, 80) * mm});
            skArc(sketch, "E79.18", {"start": v(80, 80) * mm, "mid": v(77.07, 87.07) * mm, "end": v(70, 90) * mm});
            skLineSegment(sketch, "E80", {"start": v(0, 90) * mm, "end": v(0, 120) * mm, "construction": true});
            skCircle(sketch, "E81", {"center": v(0, 120) * mm, "radius": 6 * mm});
            skArc(sketch, "E82", {"start": v(15, 120) * mm, "mid": v(0, 135) * mm, "end": v(-15, 120) * mm});
            skLineSegment(sketch, "E83", {"start": v(-15, 120) * mm, "end": v(-15, 108) * mm});
            skLineSegment(sketch, "E84", {"start": v(-15, 108) * mm, "end": v(-33, 90) * mm});
            skLineSegment(sketch, "E85", {"start": v(15, 120) * mm, "end": v(15, 108) * mm});
            skLineSegment(sketch, "E86", {"start": v(15, 108) * mm, "end": v(33, 90) * mm});
            skLineSegment(sketch, "E87", {"start": v(-80, 0) * mm, "end": v(80, 0) * mm, "construction": true});
            skLineSegment(sketch, "E88.MirrorCS", {"start": v(-15, -108) * mm, "end": v(-33, -90) * mm});
            skLineSegment(sketch, "E89.MirrorCS", {"start": v(15, -120) * mm, "end": v(15, -108) * mm});
            skCircle(sketch, "E90.MirrorC", {"center": v(0, -120) * mm, "radius": 6 * mm});
            skLineSegment(sketch, "E91.MirrorCS", {"start": v(-15, -120) * mm, "end": v(-15, -108) * mm});
            skArc(sketch, "E92.MirrorCS", {"start": v(15, -120) * mm, "mid": v(0, -135) * mm, "end": v(-15, -120) * mm});
            skLineSegment(sketch, "E93.MirrorCS", {"start": v(0, -90) * mm, "end": v(0, -120) * mm, "construction": true});
            skLineSegment(sketch, "E94.MirrorCS", {"start": v(15, -108) * mm, "end": v(33, -90) * mm});
            skCircle(sketch, "E95.0", {"center": v(60, 67.5) * mm, "radius": 4 * mm});
            skSolve(sketch);
        }
        {
            var Q0;
            Q0 = qSketchRegion(id + "F16", true);
            var Q1;
            Q1=makeQuery(id+"F2.opExtrude","CAP_FACE",FACE,{"disambiguationData":[OSD([sQuery(id+"F0.wireOp",EDGE,"E12"),sQuery(id+"F0.wireOp",EDGE,"E13"),sQuery(id+"F0.wireOp",EDGE,"E14"),sQuery(id+"F0.wireOp",EDGE,"E15"),sQuery(id+"F0.wireOp",EDGE,"E17.filletArc"),sQuery(id+"F0.wireOp",EDGE,"E18.filletArc"),sQuery(id+"F0.wireOp",EDGE,"E19.filletArc"),sQuery(id+"F0.wireOp",EDGE,"E20.filletArc"),sQuery(id+"F0.wireOp",EDGE,"E25.0"),sQuery(id+"F0.wireOp",EDGE,"E25.1"),sQuery(id+"F0.wireOp",EDGE,"E25.2"),sQuery(id+"F0.wireOp",EDGE,"E25.3"),sQuery(id+"F0.wireOp",EDGE,"E25.4"),sQuery(id+"F0.wireOp",EDGE,"E25.5"),sQuery(id+"F0.wireOp",EDGE,"E25.6"),sQuery(id+"F0.wireOp",EDGE,"E25.7")])],"isStart":false});
            extrude(context, id + "F17", {"entities" : qUnion([Q0]), "endBound" : BoundingType.UP_TO_SURFACE, "depth" : 25 * mm, "endBoundEntityFace" : qUnion([Q1]), "offsetDistance" : 25 * mm});
        }
    });
